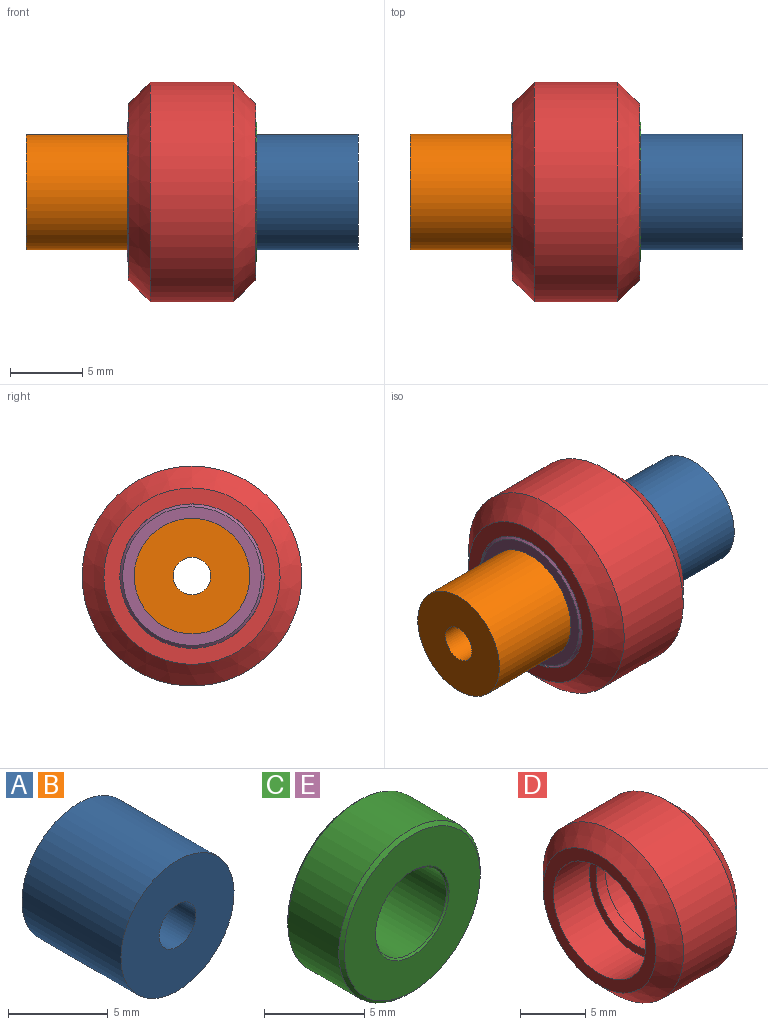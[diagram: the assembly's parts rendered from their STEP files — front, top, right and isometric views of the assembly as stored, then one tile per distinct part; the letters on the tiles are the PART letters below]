
ASSEMBLY  parts=5 mates=4
PART A: 4 faces, bbox 8x7x8 mm
  f0: cylinder r=1.3mm len=7mm, axis (0,1,0), area 57.2mm2, adj f2,f3
  f1: cylinder r=4mm len=8mm, axis (0,1,0), area 175.9mm2, adj f2,f3
  f2: plane 8x8mm, normal (0,-1,0), area 45mm2, adj f0,f1
  f3: plane 8x8mm, normal (0,1,0), area 45mm2, adj f0,f1
PART B: same geometry as A
PART C: 8 faces, bbox 10x4x10 mm
  f0: cylinder r=2.5mm len=5mm, axis (0,1,0), area 59.7mm2, adj f6,f7
  f1: cylinder r=5mm len=10mm, axis (0,1,0), area 113.1mm2, adj f4,f5
  f2: plane 9.6x9.6mm, normal (0,-1,0), area 51.1mm2, adj f5,f7
  f3: plane 9.6x9.6mm, normal (0,1,0), area 51.1mm2, adj f4,f6
  f4: cone r=5mm half-angle=45deg, axis (0,-1,0), area 8.7mm2, adj f1,f3
  f5: cone r=4.8mm half-angle=45deg, axis (0,1,0), area 8.7mm2, adj f1,f2
  f6: cone r=2.6mm half-angle=45deg, axis (0,1,0), area 2.3mm2, adj f0,f3
  f7: cone r=2.5mm half-angle=45deg, axis (0,-1,0), area 2.3mm2, adj f0,f2
PART D: 10 faces, bbox 8.8x15.2x15.2 mm
  f0: plane 10x10mm, normal (-1,0,0), area 21.3mm2, adj f1,f9
  f1: cylinder r=4.27mm len=8.54mm, axis (-1,0,0), area 26.8mm2, adj f0,f2
  f2: plane 10x10mm, normal (1,0,0), area 21.3mm2, adj f1,f3
  f3: cylinder r=5mm len=10mm, axis (-1,0,0), area 122.5mm2, adj f2,f4
  f4: plane 12.21x12.21mm, normal (1,0,0), area 38.6mm2, adj f3,f5
  f5: cone r=6.11mm half-angle=45deg, axis (-1,0,0), area 92mm2, adj f4,f6
  f6: cylinder r=7.62mm len=15.23mm, axis (-1,0,0), area 276.6mm2, adj f5,f7
  f7: cone r=7.62mm half-angle=45deg, axis (1,0,0), area 92mm2, adj f6,f8
  f8: plane 12.21x12.21mm, normal (-1,0,0), area 38.6mm2, adj f7,f9
  f9: cylinder r=5mm len=10mm, axis (-1,0,0), area 122.5mm2, adj f0,f8
PART E: same geometry as C
PLACE A rot(axis=(0,0,-1),90deg) t=(6.16,-0.91,-1.98)mm
PLACE B rot(axis=(0,0,-1),90deg) t=(-9.84,-0.91,-1.98)mm
PLACE C rot(axis=(0.58,0.58,-0.58),120deg) t=(-0.84,-0.91,-1.98)mm
PLACE D t=(-5.34,-0.91,-1.98)mm fixed
PLACE E rot(axis=(-0.58,-0.58,-0.58),120deg) t=(-5.84,-0.91,-1.98)mm
MATE fastened D.f1 <-> E.f1  axis (-1,0,0) through (-5.84,-0.91,-1.98)mm
MATE fastened E.f1 <-> B.f1  axis (-1,0,0) through (-9.84,-0.91,-1.98)mm
MATE fastened D.f1 <-> C.f1  axis (1,0,0) through (-4.84,-0.91,-1.98)mm
MATE fastened C.f1 <-> A.f1  axis (1,0,0) through (-0.84,-0.91,-1.98)mm
